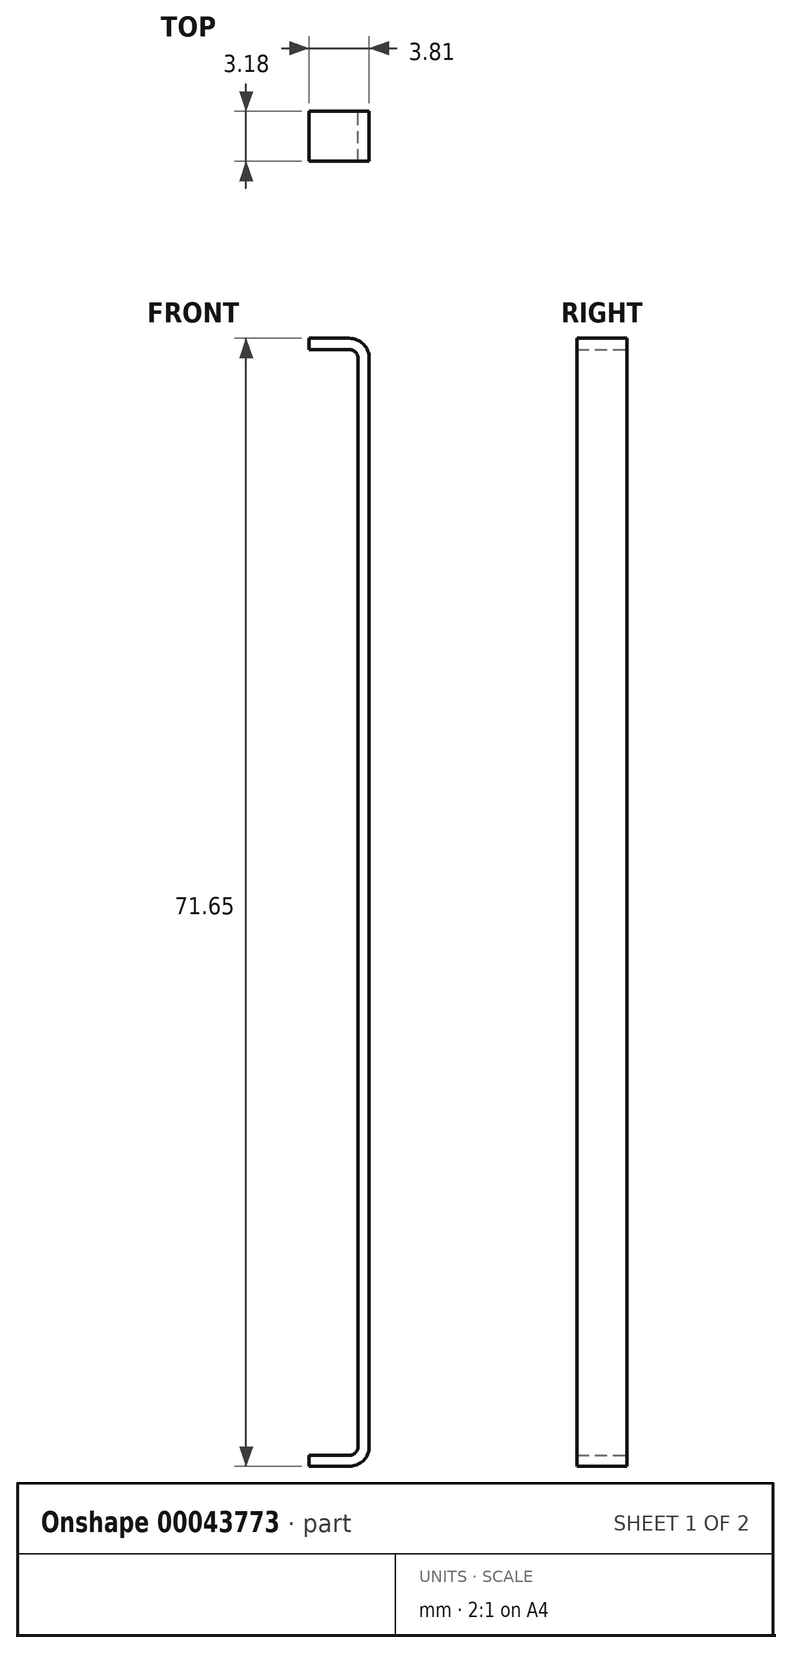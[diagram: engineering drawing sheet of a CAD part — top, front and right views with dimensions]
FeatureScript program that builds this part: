
annotation { "Feature Type Name" : "Feature", "Feature Type Description" : "" }
export const myFeature = defineFeature(function(context is Context, id is Id, definition is map)
    precondition{}
    {
        {
            var Q0;
            Q0=qCreatedBy(makeId("Front.planeOp"),FACE);
            var sketch = newSketch(context, id + "F0", { "sketchPlane" : qUnion([Q0])});
            skLineSegment(sketch, "E0", {"start": v(0, 0) * mm, "end": v(0, -71.65) * mm});
            skLineSegment(sketch, "E1", {"start": v(-0.71, -70.38) * mm, "end": v(-0.71, -1.27) * mm});
            skLineSegment(sketch, "E2", {"start": v(-3.8, -71.65) * mm, "end": v(-3.8, 0) * mm, "construction": true});
            skLineSegment(sketch, "E3.0", {"start": v(-0.71, 6.35) * mm, "end": v(-0.71, -63.5) * mm});
            skLineSegment(sketch, "E4", {"start": v(-3.8, -0.71) * mm, "end": v(-3.8, 0) * mm});
            skLineSegment(sketch, "E5", {"start": v(-1.27, -0.71) * mm, "end": v(-3.8, -0.71) * mm});
            skLineSegment(sketch, "E6", {"start": v(-3.81, 0) * mm, "end": v(0, 0) * mm});
            skLineSegment(sketch, "E7", {"start": v(0, -71.65) * mm, "end": v(-3.8, -71.65) * mm});
            skLineSegment(sketch, "E8", {"start": v(-3.8, -70.94) * mm, "end": v(-3.8, -71.65) * mm});
            skLineSegment(sketch, "E9", {"start": v(-1.27, -70.94) * mm, "end": v(-3.8, -70.94) * mm});
            skArc(sketch, "E10", {"start": v(-0.71, -1.27) * mm, "mid": v(-0.87, -0.87) * mm, "end": v(-1.27, -0.71) * mm});
            skLineSegment(sketch, "E11", {"start": v(-1.27, 0) * mm, "end": v(-1.27, -0.71) * mm, "construction": true});
            skLineSegment(sketch, "E12", {"start": v(0, -1.27) * mm, "end": v(-0.71, -1.27) * mm, "construction": true});
            skLineSegment(sketch, "E13", {"start": v(-1.27, -71.65) * mm, "end": v(-1.27, -70.94) * mm, "construction": true});
            skLineSegment(sketch, "E14", {"start": v(-0.71, -70.38) * mm, "end": v(0, -70.38) * mm, "construction": true});
            skArc(sketch, "E15", {"start": v(0, -1.27) * mm, "mid": v(-0.37, -0.37) * mm, "end": v(-1.27, 0) * mm});
            skArc(sketch, "E16", {"start": v(-1.27, -71.65) * mm, "mid": v(-0.37, -71.28) * mm, "end": v(0, -70.38) * mm});
            skArc(sketch, "E17.0", {"start": v(-1.27, -70.94) * mm, "mid": v(-0.87, -70.78) * mm, "end": v(-0.71, -70.38) * mm});
            skPoint(sketch, "E18", {"position": v(-0.71, 0) * mm});
            skLineSegment(sketch, "E19", {"start": v(-1.27, -0.71) * mm, "end": v(-0.71, -0.71) * mm, "construction": true});
            skSolve(sketch);
        }
        {
            var Q0;
            {var subQ6=sQuery(id+"F0.wireOp",EDGE,"E4");Q0=makeQuery(id+"F0.imprint","IMPRINT",FACE,{"disambiguationData":[TD([[makeQuery(id+"F0.imprint","IMPRINT",EDGE,{"derivedFrom":subQ6}),-1.0]])]});}
            var Q1;
            {var subQ9=sQuery(id+"F0.wireOp",EDGE,"E1");Q1=makeQuery(id+"F0.imprint","IMPRINT",FACE,{"disambiguationData":[TD([[makeQuery(id+"F0.imprint","IMPRINT",EDGE,{"derivedFrom":subQ9}),-1.0]])]});}
            extrude(context, id + "F1", {"entities" : qUnion([Q0, Q1]), "depth" : 3.17 * mm, "symmetric" : true});
        }
    });
